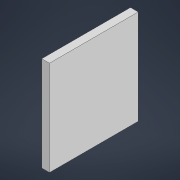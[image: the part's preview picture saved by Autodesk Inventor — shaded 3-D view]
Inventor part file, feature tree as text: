
AUTODESK INVENTOR PART (.ipt)
format: ipt  version: 2022 (Build 260153000, 153)  size: 84,992 bytes
history: native  units: mm
features: other x1, extrude x1, sketch x1
ambient origin geometry x8: Origin, YZ Plane, XZ Plane, XY Plane, X Axis, Y Axis, Z Axis, Center Point
bodies: Body1 (feature_tree)
feature tree (3):
  other  "Твердое тело1"
  extrude  "Выдавливание1"  Depth=270.0mm
  sketch  "Эскиз1"
